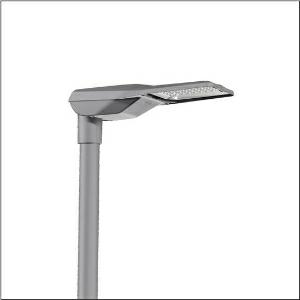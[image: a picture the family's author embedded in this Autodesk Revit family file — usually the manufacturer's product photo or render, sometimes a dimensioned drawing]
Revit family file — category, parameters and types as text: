
# Revit family: streetlight_sl_21_iq_mini___st0_8a_5xe2c31g08hb_2845
name_source: partatom
category: Lighting Fixtures
units: mm (PartAtom-declared; Revit-internal decimal feet)

## family parameters
Cut with Voids When Loaded = No
Host = Face
Light Source = No
Part Type = Normal
Room Calculation Point = No
Round Connector Dimension = Use Diameter
Shared = No

## types (1)
- --- (1 x LED, 9450 lm, 70.9 W, 3000K)
    Apparent Load = 71 VA
    CIE Flux Codes = 38 75 97 100 100
    Color Rendering = 70
    Color Temperature = 3000K
    Default Elevation = 1800 mm
    Description = Streetlight SL 21 iQ mini, mast luminaire, primary light control with lens, of PMMA, primary optical cover: cover, of toughened safety glass, transparent, light distribution: ST0.8a, light emission: direct distribution, primary light characteristic: asymmetric, installation type: post-top, side-entry, LED, High Power LED, rated luminous flux: 9.450lm, luminous efficacy: 133lm/W, light colour: 730, colour temperature: 3000K, control gear: iQ Street-Remote, control: Street-Remote, Auto-Match, Temp-Guard, Lumen-Switch, Night-Set, Smart-Wire, Light-Fading, Desk-Remote (wireless, voltage-free reading and setting of iQ features in the workshop via application-optimized NFC function/RFID function), optimised constant luminous flux control (CLO 2.0), pre-setting: linear dimming characteristic, mains connection: 220..240V, AC, 50/60Hz, start of lifetime: 71W, end of service life: 75W, reduction: 31W, luminaire housing, of diecast aluminium, powder-coated, Siteco® metallic grey (DB 702S), corrosivity category C5 mid according to DIN EN ISO 12944, please order mast flange separately, inclination adjustable: 0°, 5°, 10°, 15°, sealing non-destructively replaceable, multi-level sealing system, length: 628mm, width: 235mm, height: 110mm, mast flange for spigot size: 42mm (side-entry): 5XC10008XM4, 60/48mm (side-entry/post-top): 5XC10108XM2, 76/60mm (side-entry/post-top): 5XC10108XM1, mounting height: 4..8m, protection rating (complete): IP66, insulation class (complete): insulation class II (safety insulation), certification: CE, ENEC, ENEC+, VDE, impact resistance: IK10, permissible operating ambient temperature for outdoor applications: -40..+50°C, standard-compliant lighting for roads and squares, packaging unit: 1 piece

Light Distribution: ST0.8a
    Height = 110 mm
    Lamp = 1 x LED
    Lamp Light Flux = 9450 lm
    Lamp Power = 70.9 W
    Lamp count = 1
    Length = 625 mm
    Luminous efficacy = 133 lm/W
    Manufacturer = Siteco
    ModVariant = No
    Model = 5XE2C31G08HB
    Number of Poles = 1
    OnlyDefault = Yes
    Power Factor = 1
    Product Name = Streetlight SL 21 iQ mini | ST0.8a
    Product group = mast luminaire | pylon top
    ProductGroupID = 6100
    Protection Class = Protection class II
    Protection Degree = IP 66
    RLX_Detail_Level = 1
    RLX_Emergency_Light_Flux = 0 lm
    RLX_Emergency_Type = 0
    RLX_Emergency_Type_DB = No
    RlxData = <blob elided: 26337 chars, md5=2fa9d054>
    Socket = socket
    Standby Power = 0 W
    System Light Flux = 9450 lm
    System Power = 71 W
    Type Comments = factory setting: luminous flux: 100 % | dim-lin: 254 | 711 mA
    Type Image = l_1003519.jpg
    URL = http://relux.com
    VarID = @adj_178869
    Voltage = 0 V
    Weight = 0.00 kg
    Width = 234 mm

## geometry (parser evidence)
native form markers: Blend x4, Sweep x10
no freeform markers — native parametric forms only
